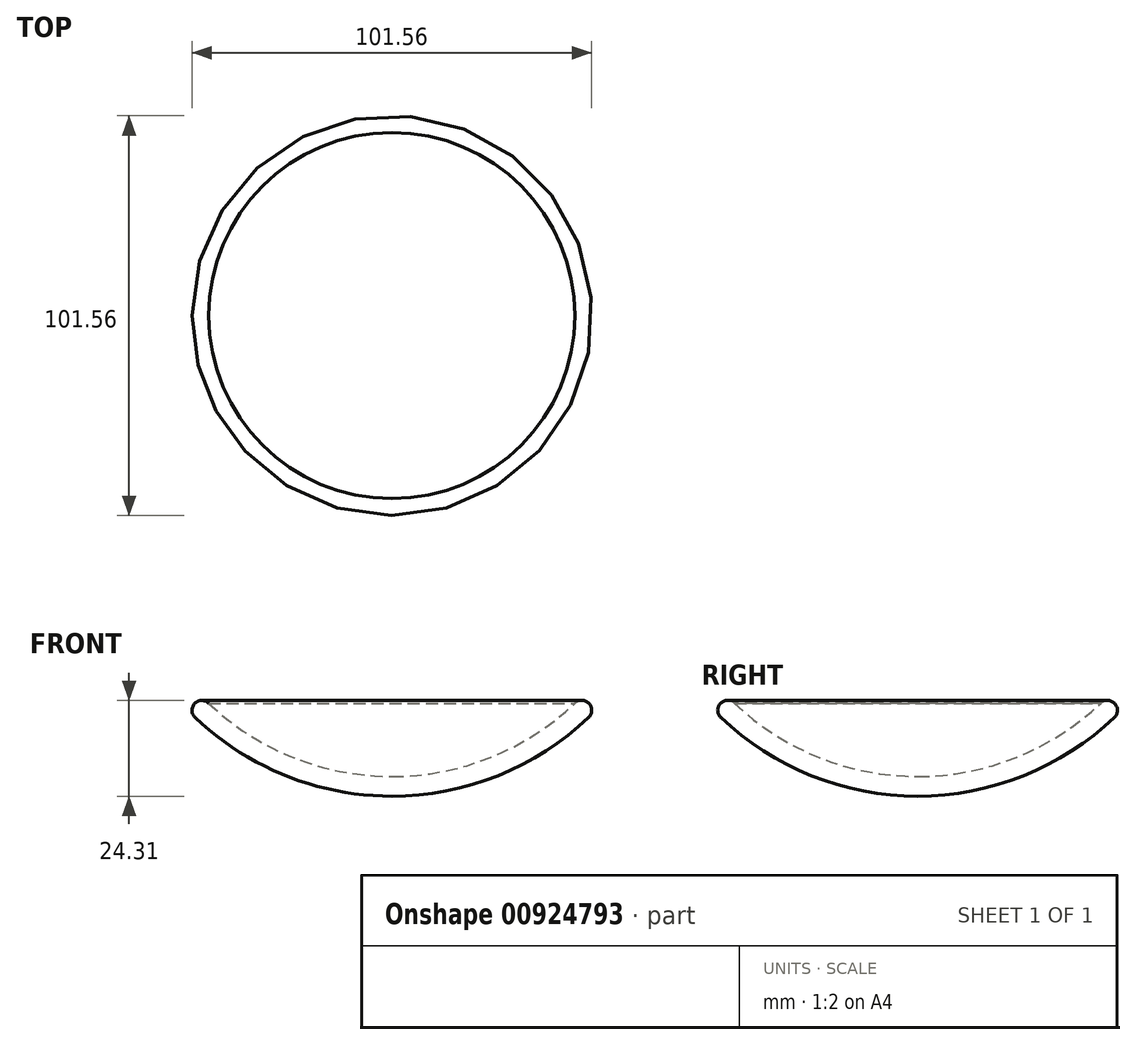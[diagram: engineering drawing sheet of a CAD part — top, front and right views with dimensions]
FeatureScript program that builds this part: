
annotation { "Feature Type Name" : "Feature", "Feature Type Description" : "" }
export const myFeature = defineFeature(function(context is Context, id is Id, definition is map)
    precondition{}
    {
        {
            var Q0;
            Q0=qCreatedBy(makeId("Front.planeOp"),FACE);
            var sketch = newSketch(context, id + "F0", { "sketchPlane" : qUnion([Q0])});
            skArc(sketch, "E0", {"start": v(-50, 20) * mm, "mid": v(-26.93, 5.19) * mm, "end": v(0, 0) * mm});
            skArc(sketch, "E1.1", {"start": v(-46.55, 23.62) * mm, "mid": v(-25.07, 9.83) * mm, "end": v(0, 5) * mm});
            skArc(sketch, "E2", {"start": v(-50, 20) * mm, "mid": v(-50.07, 23.55) * mm, "end": v(-46.52, 23.6) * mm});
            skLineSegment(sketch, "E3", {"start": v(0, 5) * mm, "end": v(0, 0) * mm});
            skSolve(sketch);
        }
        {
            var Q0;
            Q0=sQuery(id+"F0.wireOp",EDGE,"E1.1");
            var Q1;
            Q1=sQuery(id+"F0.wireOp",EDGE,"E0");
            var Q2;
            Q2=sQuery(id+"F0.wireOp",EDGE,"E2");
            var Q3;
            Q3=sQuery(id+"F0.wireOp",EDGE,"E3");
            revolve(context, id + "F1", {"bodyType" : ToolBodyType.SURFACE, "surfaceOperationType" : NewSurfaceOperationType.NEW, "surfaceEntities" : qUnion([Q0, Q1, Q2]), "axis" : qUnion([Q3]), "revolveType" : RevolveType.FULL});
        }
    });
